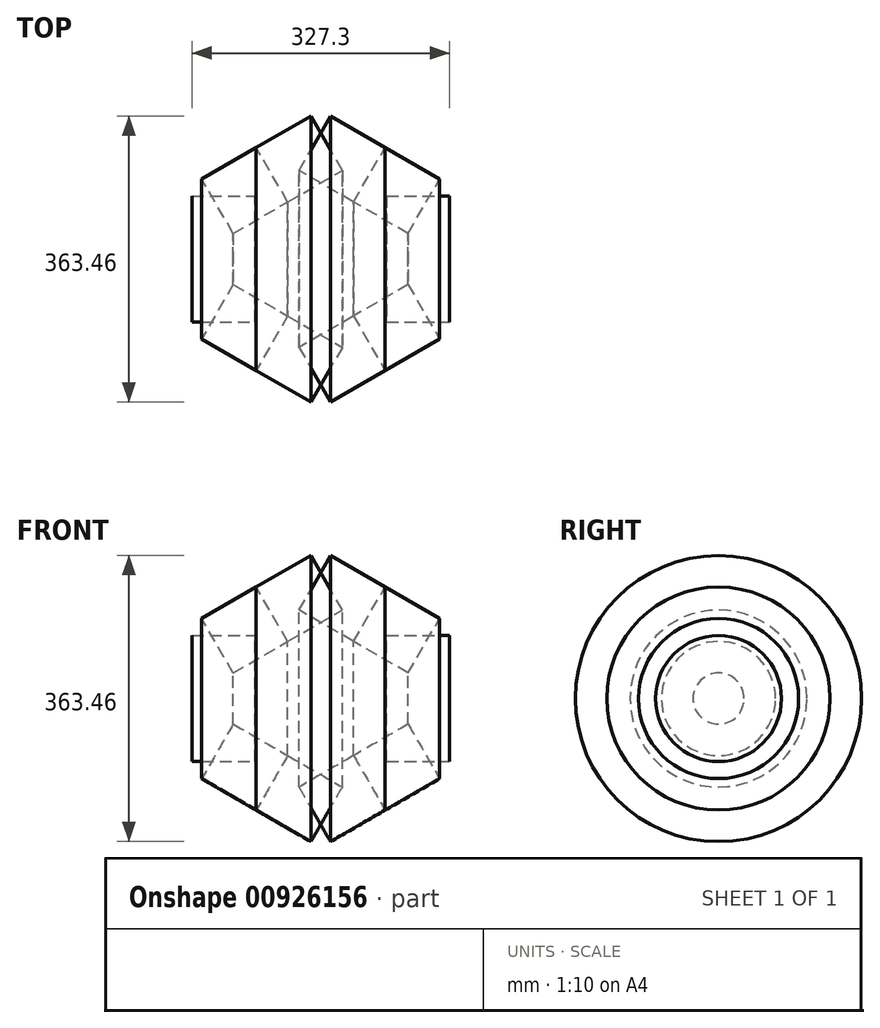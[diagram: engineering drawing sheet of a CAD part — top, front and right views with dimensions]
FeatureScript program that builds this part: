
annotation { "Feature Type Name" : "Feature", "Feature Type Description" : "" }
export const myFeature = defineFeature(function(context is Context, id is Id, definition is map)
    precondition{}
    {
        {
            var Q0;
            Q0=qCreatedBy(makeId("Front.planeOp"),FACE);
            var sketch = newSketch(context, id + "F0", { "sketchPlane" : qUnion([Q0])});
            skLineSegment(sketch, "E0.bottom", {"start": v(-80, 0) * mm, "end": v(0, 0) * mm});
            skLineSegment(sketch, "E0.top", {"start": v(-80, -80) * mm, "end": v(0, -80) * mm});
            skLineSegment(sketch, "E0.left", {"start": v(-80, 0) * mm, "end": v(-80, -80) * mm});
            skLineSegment(sketch, "E0.right", {"start": v(0, 0) * mm, "end": v(0, -80) * mm});
            skLineSegment(sketch, "E1.1.0", {"start": v(41.83, -72.44) * mm, "end": v(111.1, -112.44) * mm});
            skLineSegment(sketch, "E1.1.1", {"start": v(1.83, -141.73) * mm, "end": v(71.1, -181.73) * mm});
            skLineSegment(sketch, "E1.1.2", {"start": v(71.1, -181.73) * mm, "end": v(111.1, -112.44) * mm});
            skLineSegment(sketch, "E1.1.3", {"start": v(1.83, -141.73) * mm, "end": v(41.83, -72.44) * mm});
            skLineSegment(sketch, "E1.2.0", {"start": v(125.48, -72.44) * mm, "end": v(194.76, -32.44) * mm});
            skLineSegment(sketch, "E1.2.1", {"start": v(165.48, -141.73) * mm, "end": v(234.76, -101.73) * mm});
            skLineSegment(sketch, "E1.2.2", {"start": v(234.76, -101.73) * mm, "end": v(194.76, -32.44) * mm});
            skLineSegment(sketch, "E1.2.3", {"start": v(165.48, -141.73) * mm, "end": v(125.48, -72.44) * mm});
            skLineSegment(sketch, "E1.3.0", {"start": v(167.3, 0) * mm, "end": v(167.3, 80) * mm});
            skLineSegment(sketch, "E1.3.1", {"start": v(247.3, 0) * mm, "end": v(247.3, 80) * mm});
            skLineSegment(sketch, "E1.3.2", {"start": v(247.3, 80) * mm, "end": v(167.3, 80) * mm});
            skLineSegment(sketch, "E1.3.3", {"start": v(247.3, 0) * mm, "end": v(167.3, 0) * mm});
            skPoint(sketch, "E1.center", {"position": v(83.65, 0) * mm});
            skLineSegment(sketch, "E2.3.4.0", {"start": v(165.48, 141.73) * mm, "end": v(96.2, 181.73) * mm});
            skLineSegment(sketch, "E2.5.4.0", {"start": v(125.48, 72.44) * mm, "end": v(56.2, 112.44) * mm});
            skLineSegment(sketch, "E2.6.4.0", {"start": v(96.2, 181.73) * mm, "end": v(56.2, 112.44) * mm});
            skLineSegment(sketch, "E2.9.4.0", {"start": v(165.48, 141.73) * mm, "end": v(125.48, 72.44) * mm});
            skLineSegment(sketch, "E2.3.5.0", {"start": v(1.83, 141.73) * mm, "end": v(-67.46, 101.73) * mm});
            skLineSegment(sketch, "E2.5.5.0", {"start": v(41.83, 72.44) * mm, "end": v(-27.46, 32.44) * mm});
            skLineSegment(sketch, "E2.6.5.0", {"start": v(-67.46, 101.73) * mm, "end": v(-27.46, 32.44) * mm});
            skLineSegment(sketch, "E2.9.5.0", {"start": v(1.83, 141.73) * mm, "end": v(41.83, 72.44) * mm});
            skSolve(sketch);
        }
        {
            var Q0;
            Q0=makeQuery(id+"F0.imprint","IMPRINT",FACE,{"disambiguationData":[TD([[makeQuery(id+"F0.imprint","IMPRINT",EDGE,{"derivedFrom":sQuery(id+"F0.wireOp",EDGE,"E1.3.0")}),-1.0]])]});
            var Q1;
            Q1=makeQuery(id+"F0.imprint","IMPRINT",FACE,{"disambiguationData":[TD([[makeQuery(id+"F0.imprint","IMPRINT",EDGE,{"derivedFrom":sQuery(id+"F0.wireOp",EDGE,"E1.2.0")}),-1.0]])]});
            var Q2;
            Q2=makeQuery(id+"F0.imprint","IMPRINT",FACE,{"disambiguationData":[TD([[makeQuery(id+"F0.imprint","IMPRINT",EDGE,{"derivedFrom":sQuery(id+"F0.wireOp",EDGE,"E0.bottom")}),-1.0]])]});
            var Q3;
            Q3=makeQuery(id+"F0.imprint","IMPRINT",FACE,{"disambiguationData":[TD([[makeQuery(id+"F0.imprint","IMPRINT",EDGE,{"derivedFrom":sQuery(id+"F0.wireOp",EDGE,"E1.1.0")}),-1.0]])]});
            var Q4;
            Q4=makeQuery(id+"F0.imprint","IMPRINT",FACE,{"disambiguationData":[TD([[makeQuery(id+"F0.imprint","IMPRINT",EDGE,{"derivedFrom":sQuery(id+"F0.wireOp",EDGE,"E2.3.4.0")}),1.0]])]});
            var Q5;
            Q5=makeQuery(id+"F0.imprint","IMPRINT",FACE,{"disambiguationData":[TD([[makeQuery(id+"F0.imprint","IMPRINT",EDGE,{"derivedFrom":sQuery(id+"F0.wireOp",EDGE,"E2.3.5.0")}),1.0]])]});
            var Q6;
            Q6=sQuery(id+"F0.wireOp",EDGE,"E1.3.3");
            revolve(context, id + "F1", {"surfaceOperationType" : NewSurfaceOperationType.NEW, "entities" : qUnion([Q0, Q1, Q2, Q3, Q4, Q5]), "axis" : qUnion([Q6]), "revolveType" : RevolveType.FULL});
        }
    });
